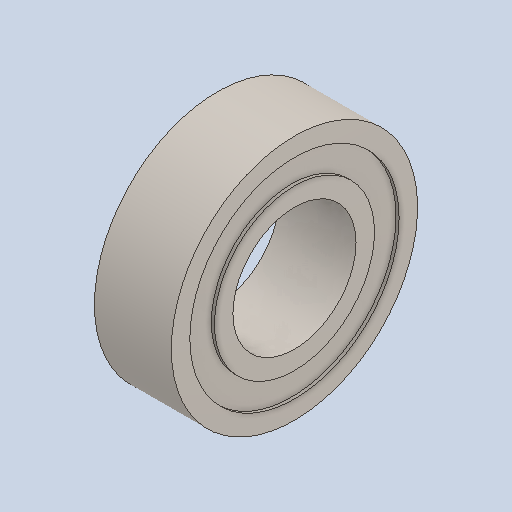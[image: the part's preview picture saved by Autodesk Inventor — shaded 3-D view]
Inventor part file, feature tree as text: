
AUTODESK INVENTOR PART (.ipt)
format: ipt  version: 2024.2 (Build 282272000, 272)  size: 134,656 bytes
history: native  units: in
note: dims shown in document units (in); Inventor stores cm internally (conversion verified against a paired STEP export)
features: revolve x1
ambient origin geometry x8: Origin, YZ Plane, XZ Plane, XY Plane, X Axis, Y Axis, Z Axis, Center Point
bodies: Solid1 (feature_tree)
feature tree (1):
  revolve  "Revolve1"  [1 undecoded]
note: 1 required parameter value undecoded (feature->parameter linkage not recoverable at this tier; creation-order binding heuristic only, values carry confidence <= 0.55)
